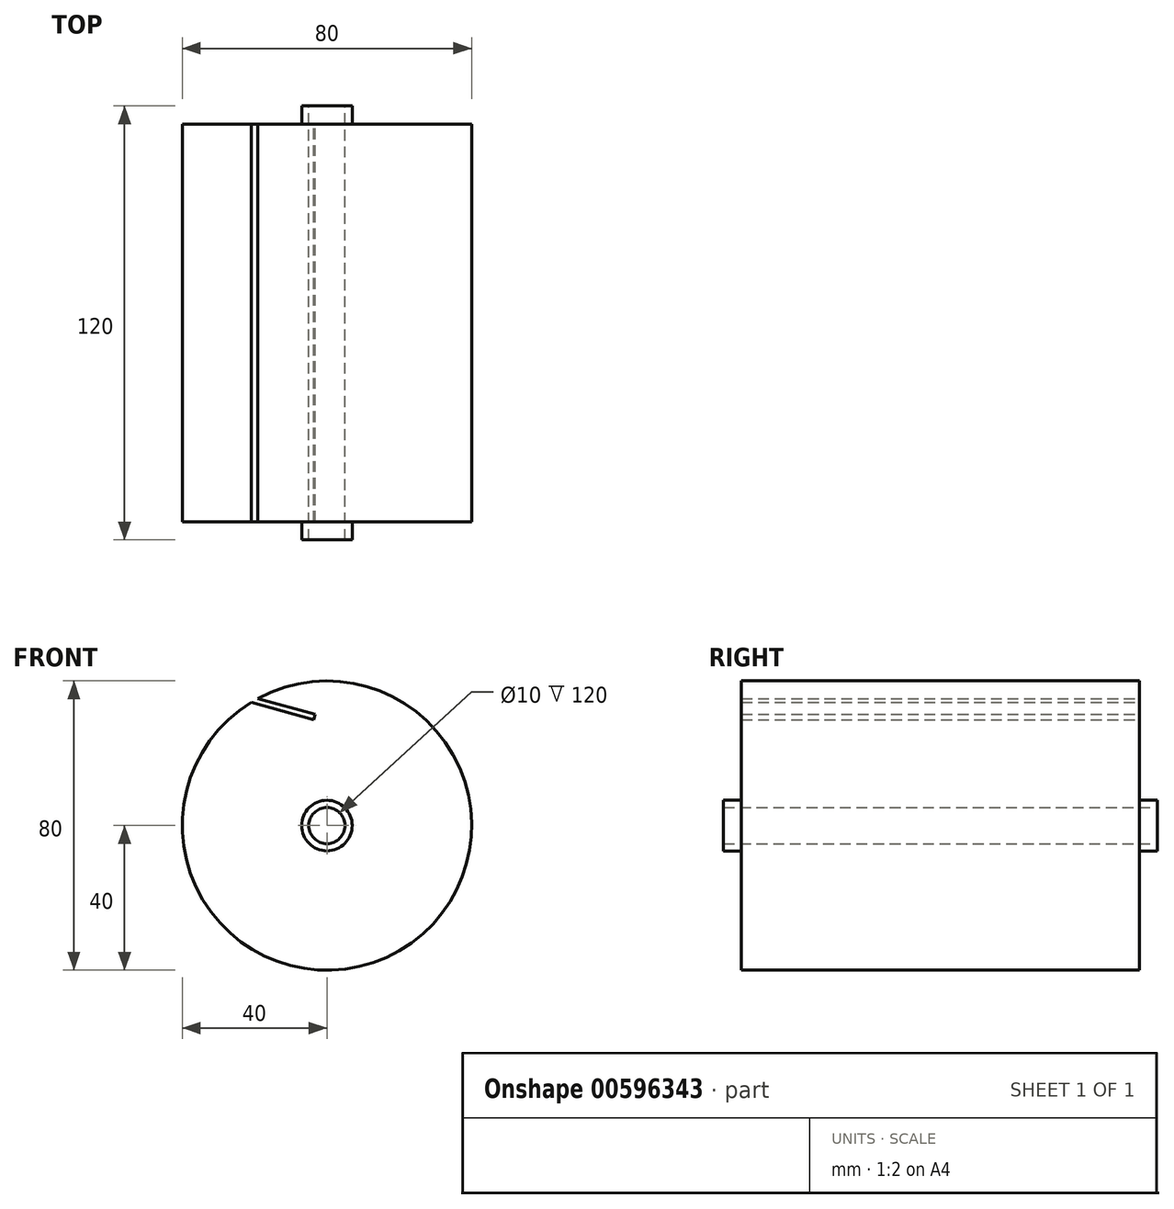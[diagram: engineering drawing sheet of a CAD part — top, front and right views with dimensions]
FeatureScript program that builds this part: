
annotation { "Feature Type Name" : "Feature", "Feature Type Description" : "" }
export const myFeature = defineFeature(function(context is Context, id is Id, definition is map)
    precondition{}
    {
        {
            var Q0;
            Q0=qCreatedBy(makeId("Front.planeOp"),FACE);
            var sketch = newSketch(context, id + "F0", { "sketchPlane" : qUnion([Q0])});
            skCircle(sketch, "E0", {"center": v(0, 0) * mm, "radius": 40 * mm});
            skCircle(sketch, "E1", {"center": v(0, 0) * mm, "radius": 5 * mm});
            skSolve(sketch);
        }
        {
            var Q0;
            Q0=makeQuery(id+"F0.imprint","IMPRINT",FACE,{"disambiguationData":[TD([[makeQuery(id+"F0.imprint","IMPRINT",EDGE,{"derivedFrom":sQuery(id+"F0.wireOp",EDGE,"E0")}),1.0]])]});
            extrude(context, id + "F1", {"entities" : qUnion([Q0]), "depth" : 110 * mm, "offsetDistance" : 25 * mm});
        }
        {
            var Q0;
            Q0=makeQuery(id+"F1.opExtrude","CAP_FACE",FACE,{"disambiguationData":[OSD([sQuery(id+"F0.wireOp",EDGE,"E0"),sQuery(id+"F0.wireOp",EDGE,"E1")])],"isStart":false});
            var sketch = newSketch(context, id + "F2", { "sketchPlane" : qUnion([Q0])});
            skCircle(sketch, "E2", {"center": v(0, 0) * mm, "radius": 7 * mm});
            skSolve(sketch);
        }
        {
            var Q0;
            Q0=makeQuery(id+"F2.imprint","IMPRINT",FACE,{"disambiguationData":[TD([[makeQuery(id+"F2.imprint","IMPRINT",EDGE,{"derivedFrom":sQuery(id+"F2.wireOp",EDGE,"E2")}),1.0]])]});
            extrude(context, id + "F3", {"entities" : qUnion([Q0]), "operationType" : NewBodyOperationType.ADD, "depth" : 5 * mm, "offsetDistance" : 25 * mm});
        }
        {
            var Q0;
            Q0=makeQuery(id+"F1.opExtrude","CAP_FACE",FACE,{"disambiguationData":[OSD([sQuery(id+"F0.wireOp",EDGE,"E0"),sQuery(id+"F0.wireOp",EDGE,"E1")])],"isStart":true});
            var sketch = newSketch(context, id + "F4", { "sketchPlane" : qUnion([Q0])});
            skCircle(sketch, "E3", {"center": v(0, 0) * mm, "radius": 7 * mm});
            skSolve(sketch);
        }
        {
            var Q0;
            Q0=makeQuery(id+"F4.imprint","IMPRINT",FACE,{"disambiguationData":[TD([[makeQuery(id+"F4.imprint","IMPRINT",EDGE,{"derivedFrom":sQuery(id+"F4.wireOp",EDGE,"E3")}),1.0]])]});
            extrude(context, id + "F5", {"entities" : qUnion([Q0]), "operationType" : NewBodyOperationType.ADD, "depth" : 5 * mm, "offsetDistance" : 25 * mm});
        }
        {
            var Q0;
            Q0=makeQuery(id+"F1.opExtrude","CAP_FACE",FACE,{"disambiguationData":[OSD([sQuery(id+"F0.wireOp",EDGE,"E0"),sQuery(id+"F0.wireOp",EDGE,"E1")])],"isStart":true});
            var sketch = newSketch(context, id + "F6", { "sketchPlane" : qUnion([Q0])});
            skLineSegment(sketch, "E4", {"start": v(20.92, 34.1) * mm, "end": v(3.6, 29.29) * mm});
            skLineSegment(sketch, "E5", {"start": v(3.6, 29.29) * mm, "end": v(3.2, 30.73) * mm});
            skLineSegment(sketch, "E6", {"start": v(3.2, 30.73) * mm, "end": v(19.1, 35.14) * mm});
            skLineSegment(sketch, "E7", {"start": v(19.1, 35.14) * mm, "end": v(20.92, 35.6) * mm});
            skLineSegment(sketch, "E8", {"start": v(20.92, 35.6) * mm, "end": v(20.92, 34.1) * mm});
            skSolve(sketch);
        }
        {
            var Q0;
            {var subQ0=sQuery(id+"F6.wireOp",EDGE,"E4");Q0=makeQuery(id+"F6.imprint","IMPRINT",FACE,{"disambiguationData":[TD([[makeQuery(id+"F6.imprint","IMPRINT",EDGE,{"derivedFrom":subQ0}),-1.0]])]});}
            var Q1;
            {var subQ0=sQuery(id+"F6.wireOp",EDGE,"E7");Q1=makeQuery(id+"F6.imprint","IMPRINT",FACE,{"disambiguationData":[TD([[makeQuery(id+"F6.imprint","IMPRINT",EDGE,{"derivedFrom":subQ0}),-1.0]])]});}
            var Q2;
            Q2=makeQuery(id+"F1.opExtrude","CAP_FACE",FACE,{"disambiguationData":[OSD([sQuery(id+"F0.wireOp",EDGE,"E0"),sQuery(id+"F0.wireOp",EDGE,"E1")])],"isStart":false});
            extrude(context, id + "F7", {"entities" : qUnion([Q0, Q1]), "operationType" : NewBodyOperationType.REMOVE, "endBound" : BoundingType.UP_TO_SURFACE, "oppositeDirection" : true, "depth" : 25 * mm, "endBoundEntityFace" : qUnion([Q2]), "offsetDistance" : 25 * mm});
        }
    });
